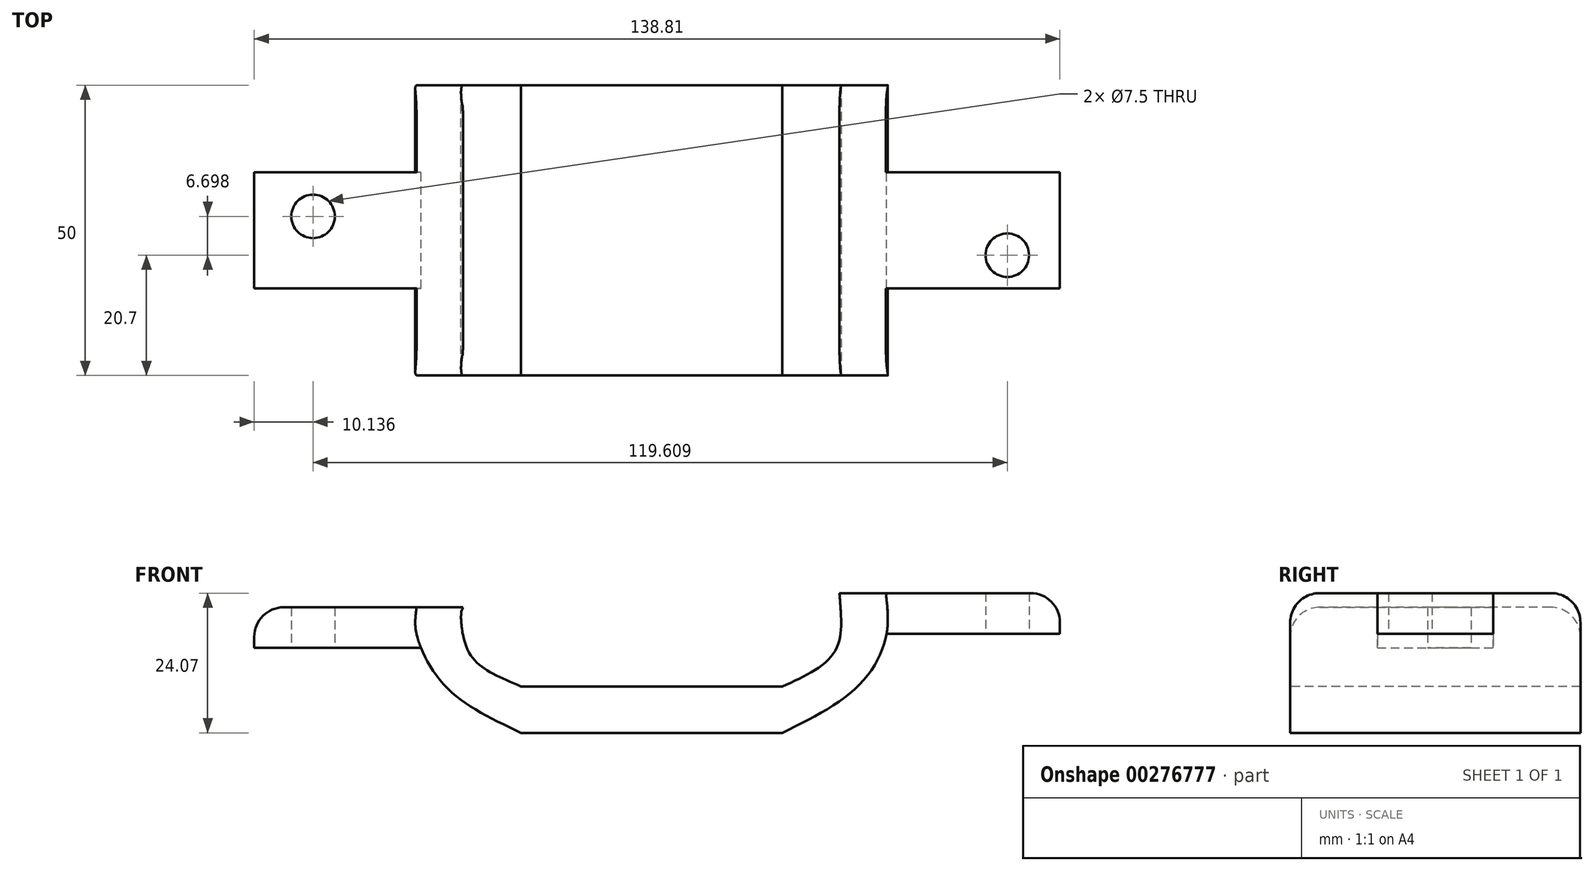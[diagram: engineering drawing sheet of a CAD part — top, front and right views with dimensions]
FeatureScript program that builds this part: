
annotation { "Feature Type Name" : "Feature", "Feature Type Description" : "" }
export const myFeature = defineFeature(function(context is Context, id is Id, definition is map)
    precondition{}
    {
        {
            var Q0;
            Q0=qCreatedBy(makeId("Front.planeOp"),FACE);
            var sketch = newSketch(context, id + "F0", { "sketchPlane" : qUnion([Q0])});
            skPoint(sketch, "E0.middle", {"position": v(26.94, 2.44) * mm});
            skLineSegment(sketch, "E1", {"start": v(-9, -14.63) * mm, "end": v(36, -14.63) * mm});
            skLineSegment(sketch, "E2", {"start": v(-19, 7) * mm, "end": v(-27, 7) * mm});
            skFitSpline(sketch, "E3", {"points": [v(-9, -14.63) * mm, v(-22, -6.63) * mm, v(-27, 2.44) * mm, v(-27, 7) * mm], "startDerivative": vector(-35.54, 17.11) * mm, "endDerivative": vector(2.54, 22.06) * mm});
            skFitSpline(sketch, "E4", {"points": [v(36, -14.63) * mm, v(49, -6.63) * mm, v(54, 2.44) * mm, v(53.85, 9.44) * mm], "startDerivative": vector(35.54, 17.11) * mm, "endDerivative": vector(-2.54, 22.06) * mm});
            skFitSpline(sketch, "E5", {"points": [v(-19, 7) * mm, v(-19.22, 6.5) * mm, v(-18.07, -0.57) * mm, v(-9, -6.63) * mm], "startDerivative": vector(-1.25, -8.06) * mm, "endDerivative": vector(24.82, -10.78) * mm});
            skLineSegment(sketch, "E6", {"start": v(53.85, 9.44) * mm, "end": v(45.85, 9.44) * mm});
            skFitSpline(sketch, "E7", {"points": [v(45.85, 9.44) * mm, v(46.07, 6.5) * mm, v(45.08, -0.57) * mm, v(36, -6.63) * mm], "startDerivative": vector(1.15, -8.05) * mm, "endDerivative": vector(-25.06, -10.75) * mm});
            skLineSegment(sketch, "E8", {"start": v(-9, -6.63) * mm, "end": v(36, -6.63) * mm});
            skLineSegment(sketch, "E9", {"start": v(53.85, 9.44) * mm, "end": v(83.85, 9.44) * mm});
            skLineSegment(sketch, "E10", {"start": v(83.85, 9.44) * mm, "end": v(83.85, 2.44) * mm});
            skLineSegment(sketch, "E11", {"start": v(83.85, 2.44) * mm, "end": v(54, 2.44) * mm});
            skLineSegment(sketch, "E12", {"start": v(-27, 7) * mm, "end": v(-54.96, 7) * mm});
            skLineSegment(sketch, "E13", {"start": v(-54.96, 7) * mm, "end": v(-54.96, 0) * mm});
            skLineSegment(sketch, "E14", {"start": v(-54.96, 0) * mm, "end": v(-26.24, 0) * mm});
            skSolve(sketch);
        }
        {
            var Q0;
            {var subQ3=sQuery(id+"F0.wireOp",EDGE,"E1");Q0=makeQuery(id+"F0.imprint","IMPRINT",FACE,{"disambiguationData":[TD([[makeQuery(id+"F0.imprint","IMPRINT",EDGE,{"derivedFrom":subQ3}),1.0]])]});}
            extrude(context, id + "F1", {"entities" : qUnion([Q0]), "oppositeDirection" : true, "depth" : 15 * mm});
        }
        {
            var Q0;
            Q0 = qSketchRegion(id + "F0", true);
            extrude(context, id + "F2", {"entities" : qUnion([Q0]), "operationType" : NewBodyOperationType.ADD, "depth" : 20 * mm});
        }
        {
            var Q0;
            {var subQ3=sQuery(id+"F0.wireOp",EDGE,"E1");Q0=makeQuery(id+"F0.imprint","IMPRINT",FACE,{"disambiguationData":[TD([[makeQuery(id+"F0.imprint","IMPRINT",EDGE,{"derivedFrom":subQ3}),1.0]])]});}
            extrude(context, id + "F3", {"entities" : qUnion([Q0]), "operationType" : NewBodyOperationType.ADD, "depth" : 35 * mm});
        }
        {
            var Q0;
            Q0=qCreatedBy(makeId("Top.planeOp"),FACE);
            var sketch = newSketch(context, id + "F4", { "sketchPlane" : qUnion([Q0])});
            skCircle(sketch, "E15", {"center": v(-44.82, -7.6) * mm, "radius": 3 * mm});
            skCircle(sketch, "E16", {"center": v(74.79, -14.3) * mm, "radius": 3 * mm});
            skSolve(sketch);
        }
        {
            var Q0;
            Q0=makeQuery(id+"F2.opExtrude","SWEPT_EDGE",EDGE,{"disambiguationData":[OSD([sQuery(id+"F0.wireOp",EDGE,"E9"),sQuery(id+"F0.wireOp",EDGE,"E10")])]});
            fillet(context, id + "F5", {"entities" : qUnion([Q0]), "radius" : 5.08 * mm, "tangentPropagation" : true, "allowEdgeOverflow" : false});
        }
        {
            var Q0;
            Q0=makeQuery(id+"F2.opExtrude","SWEPT_EDGE",EDGE,{"disambiguationData":[OSD([sQuery(id+"F0.wireOp",EDGE,"E12"),sQuery(id+"F0.wireOp",EDGE,"E13")])]});
            var Q1;
            Q1=makeQuery(id+"F3.opExtrude","CAP_EDGE",EDGE,{"disambiguationData":[OSD([sQuery(id+"F0.wireOp",EDGE,"E6")])],"isStart":false});
            fillet(context, id + "F6", {"entities" : qUnion([Q0, Q1]), "radius" : 5.08 * mm, "tangentPropagation" : true, "allowEdgeOverflow" : false});
        }
        {
            var Q0;
            Q0=makeQuery(id+"F3.opExtrude","CAP_EDGE",EDGE,{"disambiguationData":[OSD([sQuery(id+"F0.wireOp",EDGE,"E2")])],"isStart":false});
            fillet(context, id + "F7", {"entities" : qUnion([Q0]), "radius" : 5.08 * mm, "tangentPropagation" : true, "allowEdgeOverflow" : false});
        }
        {
            var Q0;
            Q0=makeQuery(id+"F1.opExtrude","CAP_EDGE",EDGE,{"disambiguationData":[OSD([sQuery(id+"F0.wireOp",EDGE,"E2")])],"isStart":false});
            fillet(context, id + "F8", {"entities" : qUnion([Q0]), "radius" : 5.08 * mm, "tangentPropagation" : true, "allowEdgeOverflow" : false});
        }
        {
            var Q0;
            Q0=makeQuery(id+"F1.opExtrude","CAP_EDGE",EDGE,{"disambiguationData":[OSD([sQuery(id+"F0.wireOp",EDGE,"E6")])],"isStart":false});
            fillet(context, id + "F9", {"entities" : qUnion([Q0]), "radius" : 5.08 * mm, "tangentPropagation" : true, "allowEdgeOverflow" : false});
        }
        {
            var Q0;
            Q0=sQuery(id+"F4.wireOp",VERTEX,"E15.center");
            var Q1;
            Q1=sQuery(id+"F4.wireOp",VERTEX,"E16.center");
            var Q2;
            Q2=makeQuery(id+"F1.opExtrude","SWEPT_BODY",BODY,{"disambiguationData":[OSD([sQuery(id+"F0.wireOp",EDGE,"E1"),sQuery(id+"F0.wireOp",EDGE,"E2"),sQuery(id+"F0.wireOp",EDGE,"E3"),sQuery(id+"F0.wireOp",EDGE,"E4"),sQuery(id+"F0.wireOp",EDGE,"E5"),sQuery(id+"F0.wireOp",EDGE,"E6"),sQuery(id+"F0.wireOp",EDGE,"E7"),sQuery(id+"F0.wireOp",EDGE,"E8")])]});
            hole(context, id + "F10", {"style" : HoleStyle.SIMPLE, "endStyle" : HoleEndStyle.THROUGH, "oppositeDirection" : true, "holeDiameter" : 7.5 * mm, "tappedDepth" : 12.7 * mm, "tapClearance" : 3, "locations" : qUnion([Q0, Q1]), "scope" : qUnion([Q2])});
        }
    });
